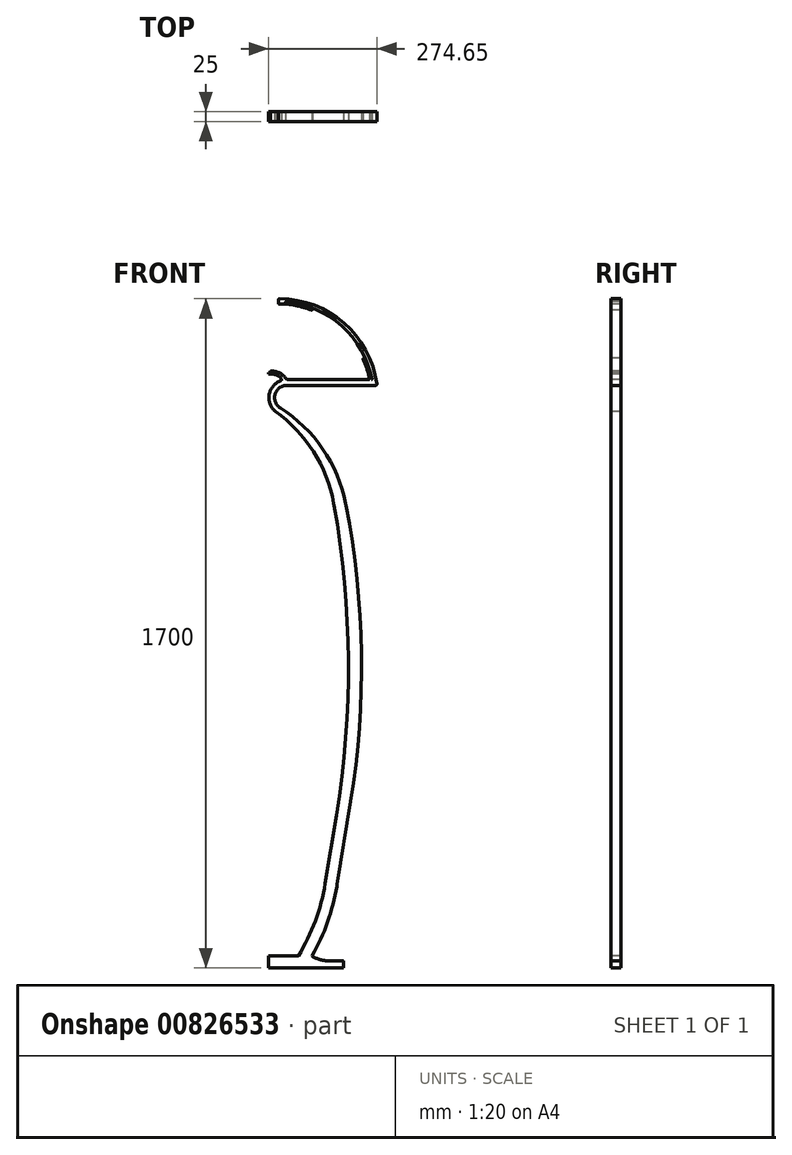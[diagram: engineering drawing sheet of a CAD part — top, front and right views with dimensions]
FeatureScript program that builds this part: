
annotation { "Feature Type Name" : "Feature", "Feature Type Description" : "" }
export const myFeature = defineFeature(function(context is Context, id is Id, definition is map)
    precondition{}
    {
        {
            var Q0;
            Q0=qCreatedBy(makeId("Front.planeOp"),FACE);
            var sketch = newSketch(context, id + "F0", { "sketchPlane" : qUnion([Q0])});
            skLineSegment(sketch, "E0", {"start": v(190, 0) * mm, "end": v(190, 15.5) * mm});
            skLineSegment(sketch, "E1", {"start": v(187.5, 18) * mm, "end": v(150, 18) * mm});
            skPoint(sketch, "E2.visualSharp", {"position": v(190, 18) * mm});
            skArc(sketch, "E2.filletArc", {"start": v(190, 15.5) * mm, "mid": v(189.27, 17.27) * mm, "end": v(187.5, 18) * mm});
            skLineSegment(sketch, "E3", {"start": v(110, 0) * mm, "end": v(110, 30) * mm, "construction": true});
            skArc(sketch, "E4", {"start": v(110.8, 29.48) * mm, "mid": v(129.57, 20.93) * mm, "end": v(150, 18) * mm});
            skLineSegment(sketch, "E5", {"start": v(0, 30) * mm, "end": v(74.44, 30) * mm});
            skLineSegment(sketch, "E6", {"start": v(0, 30) * mm, "end": v(0, 0) * mm});
            skArc(sketch, "E7", {"start": v(110.46, 30.82) * mm, "mid": v(149.36, 116.42) * mm, "end": v(172.83, 207.46) * mm});
            skArc(sketch, "E8.0", {"start": v(75.3, 30.48) * mm, "mid": v(118.21, 118.97) * mm, "end": v(143.35, 214.05) * mm});
            skPoint(sketch, "E9.visualSharp", {"position": v(110, 30) * mm});
            skArc(sketch, "E9.filletArc", {"start": v(110.46, 30.82) * mm, "mid": v(110.36, 30.08) * mm, "end": v(110.8, 29.48) * mm});
            skPoint(sketch, "E10.visualSharp", {"position": v(75, 30) * mm});
            skArc(sketch, "E10.filletArc", {"start": v(74.44, 30) * mm, "mid": v(74.93, 30.13) * mm, "end": v(75.3, 30.48) * mm});
            skArc(sketch, "E11", {"start": v(195, 1180) * mm, "mid": v(137.12, 1318.2) * mm, "end": v(29.36, 1422.28) * mm});
            skArc(sketch, "E12", {"start": v(46.11, 1480) * mm, "mid": v(16.06, 1457.43) * mm, "end": v(29.36, 1422.28) * mm});
            skLineSegment(sketch, "E13", {"start": v(0.5, 1700) * mm, "end": v(25.5, 1700) * mm, "construction": true});
            skArc(sketch, "E14", {"start": v(274.63, 1482.84) * mm, "mid": v(191.1, 1637.78) * mm, "end": v(26.45, 1700) * mm});
            skArc(sketch, "E15", {"start": v(262.41, 1495.51) * mm, "mid": v(185.73, 1630.43) * mm, "end": v(43.68, 1692.94) * mm});
            skLineSegment(sketch, "E16", {"start": v(0, 1661.22) * mm, "end": v(110, 1661.22) * mm, "construction": true});
            skLineSegment(sketch, "E17", {"start": v(110.38, 1671.64) * mm, "end": v(111.15, 1673.48) * mm});
            skLineSegment(sketch, "E18", {"start": v(240.23, 1548.12) * mm, "end": v(242.14, 1548.76) * mm});
            skArc(sketch, "E19.trimOffspring", {"start": v(110.6, 1674.8) * mm, "mid": v(77.62, 1685.25) * mm, "end": v(43.5, 1690.95) * mm});
            skArc(sketch, "E20.trimOffspring", {"start": v(109.09, 1671.1) * mm, "mid": v(68.15, 1682.9) * mm, "end": v(25.7, 1686.59) * mm});
            skArc(sketch, "E21", {"start": v(165, 1180) * mm, "mid": v(113.96, 1311.3) * mm, "end": v(17.02, 1413.5) * mm});
            skLineSegment(sketch, "E22", {"start": v(25.44, 1699.06) * mm, "end": v(24.7, 1687.65) * mm});
            skLineSegment(sketch, "E23", {"start": v(42.6, 1692.13) * mm, "end": v(42.6, 1692.13) * mm});
            skPoint(sketch, "E24.visualSharp", {"position": v(25.5, 1700) * mm});
            skArc(sketch, "E24.filletArc", {"start": v(26.45, 1700) * mm, "mid": v(25.76, 1699.73) * mm, "end": v(25.44, 1699.06) * mm});
            skPoint(sketch, "E25.visualSharp", {"position": v(24.63, 1686.57) * mm});
            skArc(sketch, "E25.filletArc", {"start": v(24.7, 1687.65) * mm, "mid": v(24.97, 1686.9) * mm, "end": v(25.7, 1686.59) * mm});
            skPoint(sketch, "E26.visualSharp", {"position": v(42.77, 1693.03) * mm});
            skArc(sketch, "E26.filletArc", {"start": v(43.68, 1692.94) * mm, "mid": v(42.98, 1692.75) * mm, "end": v(42.6, 1692.13) * mm});
            skPoint(sketch, "E27.visualSharp", {"position": v(42.4, 1691.05) * mm});
            skArc(sketch, "E27.filletArc", {"start": v(42.6, 1692.13) * mm, "mid": v(42.79, 1691.34) * mm, "end": v(43.5, 1690.95) * mm});
            skPoint(sketch, "E28.visualSharp", {"position": v(111.55, 1674.42) * mm});
            skArc(sketch, "E28.filletArc", {"start": v(111.15, 1673.48) * mm, "mid": v(111.15, 1674.26) * mm, "end": v(110.6, 1674.8) * mm});
            skPoint(sketch, "E29.visualSharp", {"position": v(110, 1670.73) * mm});
            skArc(sketch, "E29.filletArc", {"start": v(109.09, 1671.1) * mm, "mid": v(109.85, 1671.1) * mm, "end": v(110.38, 1671.64) * mm});
            skPoint(sketch, "E30.visualSharp", {"position": v(243, 1549.04) * mm});
            skArc(sketch, "E30.filletArc", {"start": v(243.37, 1548.22) * mm, "mid": v(242.86, 1548.73) * mm, "end": v(242.14, 1548.76) * mm});
            skPoint(sketch, "E31.visualSharp", {"position": v(239.18, 1547.77) * mm});
            skArc(sketch, "E31.filletArc", {"start": v(240.23, 1548.12) * mm, "mid": v(239.63, 1547.57) * mm, "end": v(239.64, 1546.76) * mm});
            skArc(sketch, "E32", {"start": v(31.18, 1491.76) * mm, "mid": v(1.27, 1456.8) * mm, "end": v(17.08, 1413.59) * mm});
            skLineSegment(sketch, "E33", {"start": v(48.8, 1494.28) * mm, "end": v(253.47, 1494.28) * mm});
            skLineSegment(sketch, "E34", {"start": v(260.61, 1494.32) * mm, "end": v(261.43, 1494.32) * mm});
            skArc(sketch, "E35.trimOffspring", {"start": v(255.92, 1497.3) * mm, "mid": v(249.12, 1522.47) * mm, "end": v(239.64, 1546.76) * mm});
            skArc(sketch, "E36.trimOffspring", {"start": v(260.61, 1494.32) * mm, "mid": v(253.55, 1521.77) * mm, "end": v(243.37, 1548.22) * mm});
            skPoint(sketch, "E37.visualSharp", {"position": v(262.65, 1494.32) * mm});
            skArc(sketch, "E37.filletArc", {"start": v(261.43, 1494.32) * mm, "mid": v(262.2, 1494.68) * mm, "end": v(262.41, 1495.51) * mm});
            skLineSegment(sketch, "E38", {"start": v(272.15, 1480) * mm, "end": v(46.11, 1480) * mm});
            skPoint(sketch, "E39.visualSharp", {"position": v(275, 1480) * mm});
            skArc(sketch, "E39.filletArc", {"start": v(272.15, 1480) * mm, "mid": v(274.03, 1480.86) * mm, "end": v(274.63, 1482.84) * mm});
            skLineSegment(sketch, "E40", {"start": v(165, 1180) * mm, "end": v(165.88, 1175.08) * mm});
            skLineSegment(sketch, "E41", {"start": v(195, 1180) * mm, "end": v(195.96, 1175.1) * mm});
            skArc(sketch, "E42", {"start": v(207.9, 422.22) * mm, "mid": v(235.47, 799.19) * mm, "end": v(195.96, 1175.1) * mm});
            skArc(sketch, "E43", {"start": v(171.68, 387.57) * mm, "mid": v(202.18, 781.57) * mm, "end": v(165.88, 1175.08) * mm});
            skLineSegment(sketch, "E44", {"start": v(207.9, 422.22) * mm, "end": v(173.61, 212.24) * mm});
            skLineSegment(sketch, "E45", {"start": v(171.68, 387.57) * mm, "end": v(143.35, 214.05) * mm});
            skPoint(sketch, "E46.startSnap0", {"position": v(16.11, 1487.14) * mm});
            skLineSegment(sketch, "E47", {"start": v(0, 1512) * mm, "end": v(3, 1512) * mm});
            skLineSegment(sketch, "E48", {"start": v(4, 1513) * mm, "end": v(4, 1515) * mm});
            skArc(sketch, "E49", {"start": v(44.7, 1496.4) * mm, "mid": v(28.22, 1510.8) * mm, "end": v(6.94, 1516) * mm});
            skLineSegment(sketch, "E50", {"start": v(0, 1493.3) * mm, "end": v(22, 1493.3) * mm, "construction": true});
            skLineSegment(sketch, "E51", {"start": v(0, 1508) * mm, "end": v(9.86, 1508) * mm});
            skArc(sketch, "E52", {"start": v(32.48, 1495.44) * mm, "mid": v(22.8, 1504.65) * mm, "end": v(9.86, 1508) * mm});
            skPoint(sketch, "E53.orphan", {"position": v(0, 1516) * mm});
            skLineSegment(sketch, "E54", {"start": v(6.94, 1516) * mm, "end": v(5, 1516) * mm});
            skLineSegment(sketch, "E55", {"start": v(0, 1512) * mm, "end": v(0, 1508) * mm});
            skPoint(sketch, "E56.visualSharp", {"position": v(256.54, 1494.28) * mm});
            skArc(sketch, "E56.filletArc", {"start": v(253.47, 1494.28) * mm, "mid": v(255.42, 1495.2) * mm, "end": v(255.92, 1497.3) * mm});
            skLineSegment(sketch, "E57", {"start": v(190, 0) * mm, "end": v(0, 0) * mm});
            skLineSegment(sketch, "E58", {"start": v(173.61, 212.24) * mm, "end": v(172.83, 207.46) * mm});
            skPoint(sketch, "E59.visualSharp", {"position": v(46.11, 1494.28) * mm});
            skArc(sketch, "E59.filletArc", {"start": v(44.7, 1496.4) * mm, "mid": v(46.49, 1494.84) * mm, "end": v(48.8, 1494.28) * mm});
            skPoint(sketch, "E60.visualSharp", {"position": v(34, 1492.64) * mm});
            skArc(sketch, "E60.filletArc", {"start": v(31.18, 1491.76) * mm, "mid": v(32.72, 1493.29) * mm, "end": v(32.48, 1495.44) * mm});
            skPoint(sketch, "E61.visualSharp", {"position": v(4, 1512) * mm});
            skArc(sketch, "E61.filletArc", {"start": v(3, 1512) * mm, "mid": v(3.7, 1512.3) * mm, "end": v(4, 1513) * mm});
            skPoint(sketch, "E62.visualSharp", {"position": v(4, 1516) * mm});
            skArc(sketch, "E62.filletArc", {"start": v(5, 1516) * mm, "mid": v(4.3, 1515.7) * mm, "end": v(4, 1515) * mm});
            skSolve(sketch);
        }
        {
            var Q0;
            Q0 = qSketchRegion(id + "F0", true);
            var Q1;
            Q1 = qConstructionFilter(qBodyType(qCreatedBy(id + "F0" ,EDGE), BodyType.WIRE), ConstructionObject.NO);
            extrude(context, id + "F1", {"entities" : qUnion([Q0]), "bodyType" : ToolBodyType.SURFACE, "surfaceEntities" : qUnion([Q1]), "depth" : 25 * mm, "offsetDistance" : 25 * mm});
        }
    });
